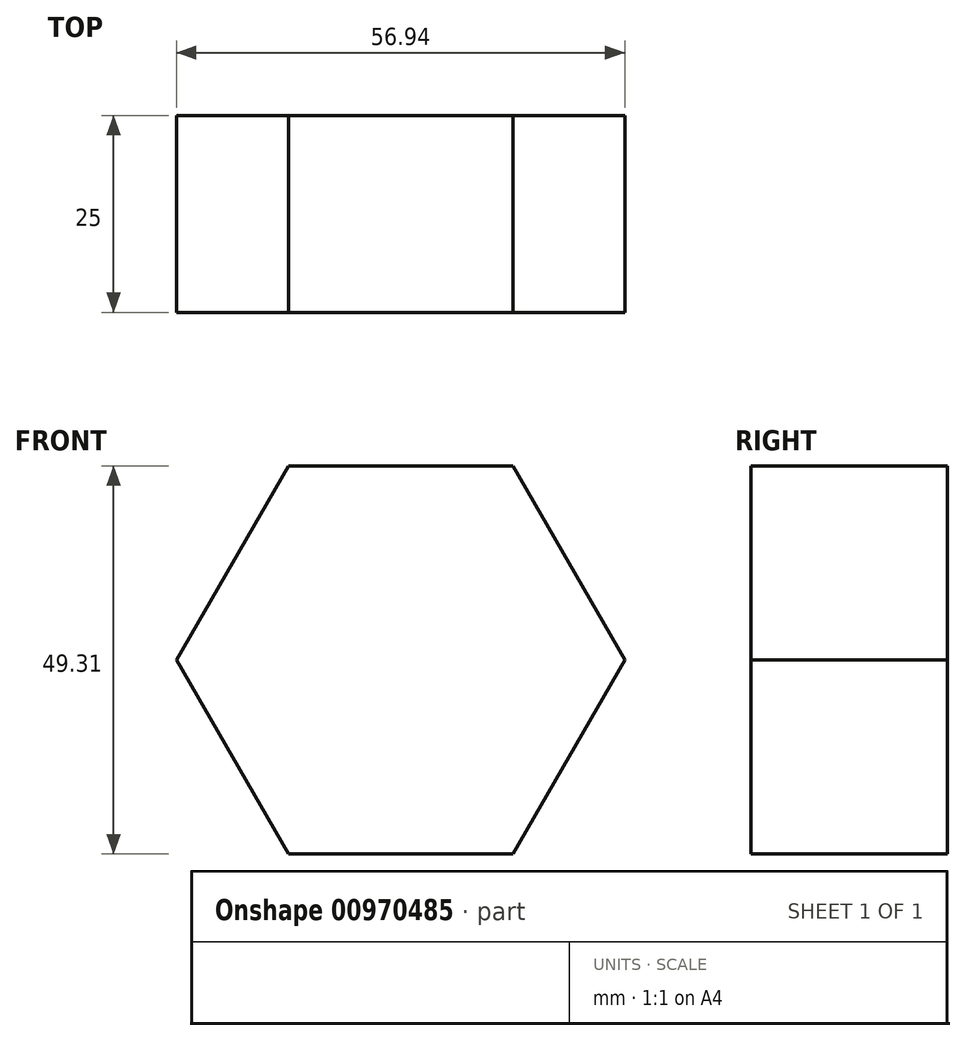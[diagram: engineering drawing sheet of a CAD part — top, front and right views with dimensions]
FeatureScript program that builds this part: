
annotation { "Feature Type Name" : "Feature", "Feature Type Description" : "" }
export const myFeature = defineFeature(function(context is Context, id is Id, definition is map)
    precondition{}
    {
        {
            var Q0;
            Q0=qCreatedBy(makeId("Front.planeOp"),FACE);
            var sketch = newSketch(context, id + "F0", { "sketchPlane" : qUnion([Q0])});
            skCircle(sketch, "E0.cCircle", {"center": v(-147.03, -2.56) * mm, "radius": 24.66 * mm, "construction": true});
            skLineSegment(sketch, "E0.0", {"start": v(-132.8, -27.21) * mm, "end": v(-161.27, -27.21) * mm});
            skLineSegment(sketch, "E0.1", {"start": v(-161.27, -27.21) * mm, "end": v(-175.5, -2.56) * mm});
            skLineSegment(sketch, "E0.2", {"start": v(-175.5, -2.56) * mm, "end": v(-161.27, 22.1) * mm});
            skLineSegment(sketch, "E0.3", {"start": v(-161.27, 22.1) * mm, "end": v(-132.8, 22.1) * mm});
            skLineSegment(sketch, "E0.4", {"start": v(-132.8, 22.1) * mm, "end": v(-118.56, -2.56) * mm});
            skLineSegment(sketch, "E0.5", {"start": v(-118.56, -2.56) * mm, "end": v(-132.8, -27.21) * mm});
            skPoint(sketch, "E0.0.midPoint", {"position": v(-147.03, -27.21) * mm});
            skSolve(sketch);
        }
        {
            var Q0;
            Q0=qSketchRegion(id+"F0",true);
            extrude(context, id + "F1", {"entities" : qUnion([Q0]), "depth" : 25 * mm, "offsetDistance" : 25 * mm});
        }
    });
